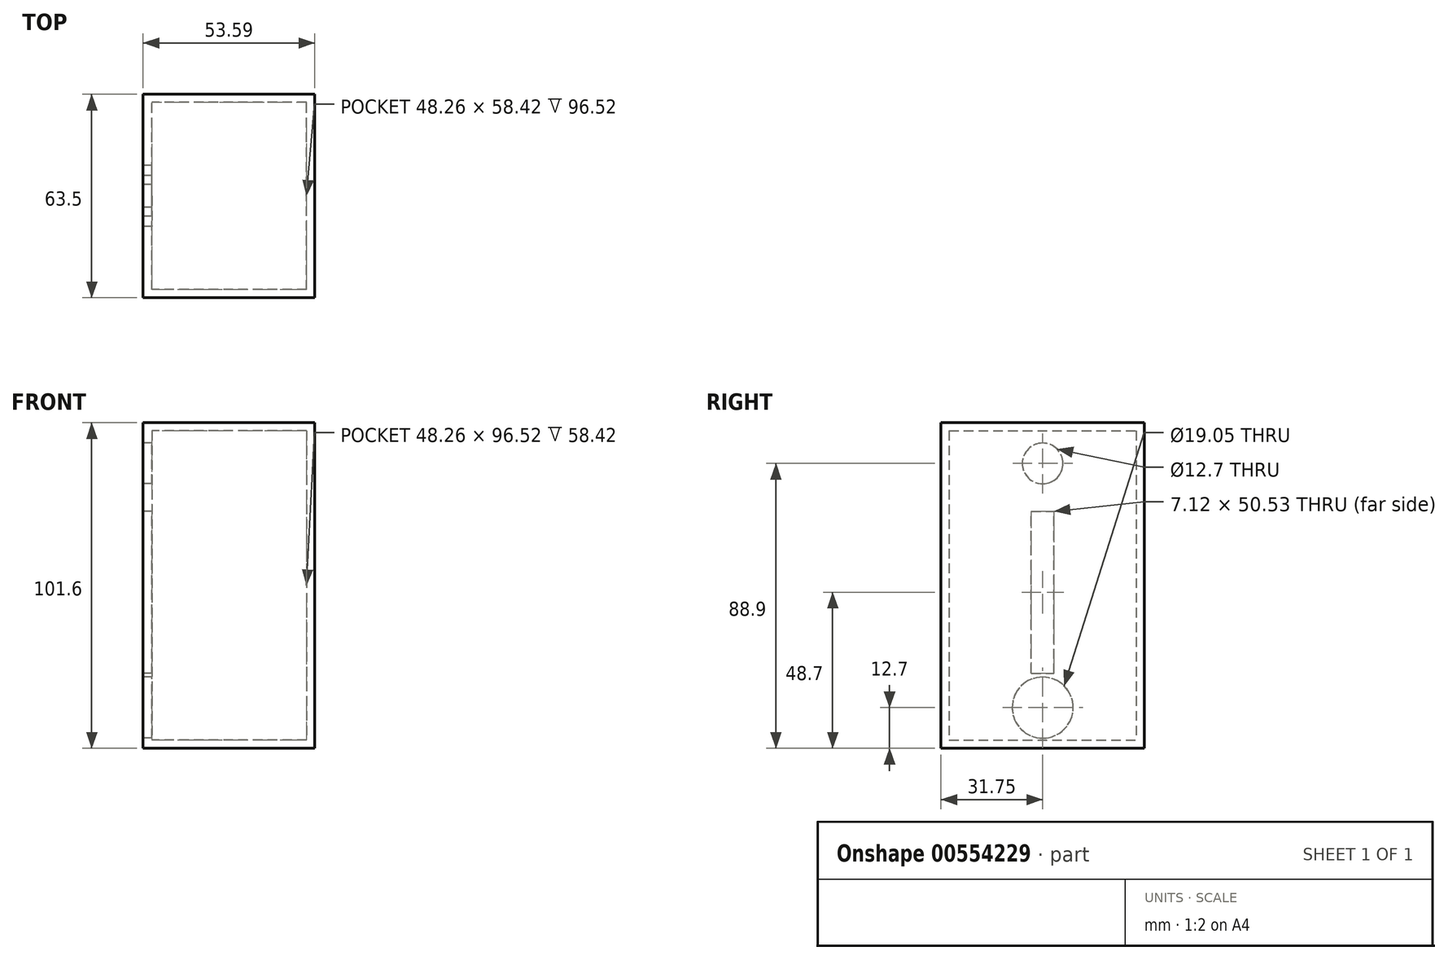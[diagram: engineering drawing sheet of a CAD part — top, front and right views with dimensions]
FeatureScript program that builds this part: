
annotation { "Feature Type Name" : "Feature", "Feature Type Description" : "" }
export const myFeature = defineFeature(function(context is Context, id is Id, definition is map)
    precondition{}
    {
        {
            var Q0;
            Q0=qCreatedBy(makeId("Right.planeOp"),FACE);
            var sketch = newSketch(context, id + "F0", { "sketchPlane" : qUnion([Q0])});
            skLineSegment(sketch, "E0.bottom", {"start": v(-31.75, 50.8) * mm, "end": v(31.75, 50.8) * mm});
            skLineSegment(sketch, "E0.top", {"start": v(-31.75, -50.8) * mm, "end": v(31.75, -50.8) * mm});
            skLineSegment(sketch, "E0.left", {"start": v(-31.75, 50.8) * mm, "end": v(-31.75, -50.8) * mm});
            skLineSegment(sketch, "E0.right", {"start": v(31.75, 50.8) * mm, "end": v(31.75, -50.8) * mm});
            skPoint(sketch, "E0.middle", {"position": v(0, 0) * mm});
            skSolve(sketch);
        }
        {
            var Q0;
            Q0=makeQuery(id+"F0.imprint","IMPRINT",FACE,{"disambiguationData":[TD([[makeQuery(id+"F0.imprint","IMPRINT",EDGE,{"derivedFrom":sQuery(id+"F0.wireOp",EDGE,"E0.bottom")}),-1.0]])]});
            extrude(context, id + "F1", {"entities" : qUnion([Q0]), "depth" : 50.8 * mm, "offsetDistance" : 25.4 * mm});
        }
        {
            var Q0;
            Q0=makeQuery(id+"F1.opExtrude","CAP_FACE",FACE,{"disambiguationData":[OSD([sQuery(id+"F0.wireOp",EDGE,"E0.bottom"),sQuery(id+"F0.wireOp",EDGE,"E0.top"),sQuery(id+"F0.wireOp",EDGE,"E0.left"),sQuery(id+"F0.wireOp",EDGE,"E0.right")])],"isStart":true});
            shell(context, id + "F2", {"entities" : qUnion([Q0]), "thickness" : 2.54 * mm});
        }
        {
            var Q0;
            Q0=qCreatedBy(makeId("Right.planeOp"),FACE);
            var sketch = newSketch(context, id + "F3", { "sketchPlane" : qUnion([Q0])});
            skLineSegment(sketch, "E1.bottom", {"start": v(31.75, 50.8) * mm, "end": v(-31.75, 50.8) * mm});
            skLineSegment(sketch, "E1.top", {"start": v(31.75, -50.8) * mm, "end": v(-31.75, -50.8) * mm});
            skLineSegment(sketch, "E1.left", {"start": v(31.75, 50.8) * mm, "end": v(31.75, -50.8) * mm});
            skLineSegment(sketch, "E1.right", {"start": v(-31.75, 50.8) * mm, "end": v(-31.75, -50.8) * mm});
            skPoint(sketch, "E1.middle", {"position": v(0, 0) * mm});
            skSolve(sketch);
        }
        {
            var Q0;
            Q0 = qSketchRegion(id + "F3", true);
            extrude(context, id + "F4", {"entities" : qUnion([Q0]), "operationType" : NewBodyOperationType.ADD, "oppositeDirection" : true, "depth" : 2.8 * mm, "offsetDistance" : 25.4 * mm});
        }
        {
            var Q0;
            Q0=makeQuery(id+"F4.opExtrude","CAP_FACE",FACE,{"disambiguationData":[OSD([sQuery(id+"F3.wireOp",EDGE,"E1.bottom"),sQuery(id+"F3.wireOp",EDGE,"E1.top"),sQuery(id+"F3.wireOp",EDGE,"E1.left"),sQuery(id+"F3.wireOp",EDGE,"E1.right")])],"isStart":false});
            var sketch = newSketch(context, id + "F5", { "sketchPlane" : qUnion([Q0])});
            skLineSegment(sketch, "E2", {"start": v(0, 0) * mm, "end": v(0, 38.1) * mm});
            skLineSegment(sketch, "E3", {"start": v(0, 0) * mm, "end": v(0, -38.1) * mm});
            skCircle(sketch, "E4", {"center": v(0, 38.1) * mm, "radius": 6.35 * mm});
            skCircle(sketch, "E5", {"center": v(0, -38.1) * mm, "radius": 9.53 * mm});
            skSolve(sketch);
        }
        {
            var Q0;
            Q0=makeQuery(id+"F5.imprint","IMPRINT",FACE,{"disambiguationData":[TD([[makeQuery(id+"F5.imprint","IMPRINT",EDGE,{"derivedFrom":sQuery(id+"F5.wireOp",EDGE,"E4")}),-1.0]])]});
            var sketch = newSketch(context, id + "F6", { "sketchPlane" : qUnion([Q0])});
            skLineSegment(sketch, "E6.bottom", {"start": v(-3.56, 23.16) * mm, "end": v(3.56, 23.16) * mm});
            skLineSegment(sketch, "E6.top", {"start": v(-3.56, -27.37) * mm, "end": v(3.56, -27.37) * mm});
            skLineSegment(sketch, "E6.left", {"start": v(-3.56, 23.16) * mm, "end": v(-3.56, -27.37) * mm});
            skLineSegment(sketch, "E6.right", {"start": v(3.56, 23.16) * mm, "end": v(3.56, -27.37) * mm});
            skPoint(sketch, "E6.middle", {"position": v(0, -2.1) * mm});
            skSolve(sketch);
        }
        {
            var Q0;
            Q0 = qSketchRegion(id + "F5", true);
            extrude(context, id + "F7", {"entities" : qUnion([Q0]), "operationType" : NewBodyOperationType.REMOVE, "oppositeDirection" : true, "depth" : 25.4 * mm, "offsetDistance" : 25.4 * mm});
        }
        {
            var Q0;
            Q0=makeQuery(id+"F6.imprint","IMPRINT",FACE,{"disambiguationData":[TD([[makeQuery(id+"F6.imprint","IMPRINT",EDGE,{"derivedFrom":sQuery(id+"F6.wireOp",EDGE,"E6.bottom")}),-1.0]])]});
            extrude(context, id + "F8", {"entities" : qUnion([Q0]), "operationType" : NewBodyOperationType.REMOVE, "oppositeDirection" : true, "depth" : 25.4 * mm, "offsetDistance" : 25.4 * mm});
        }
    });
